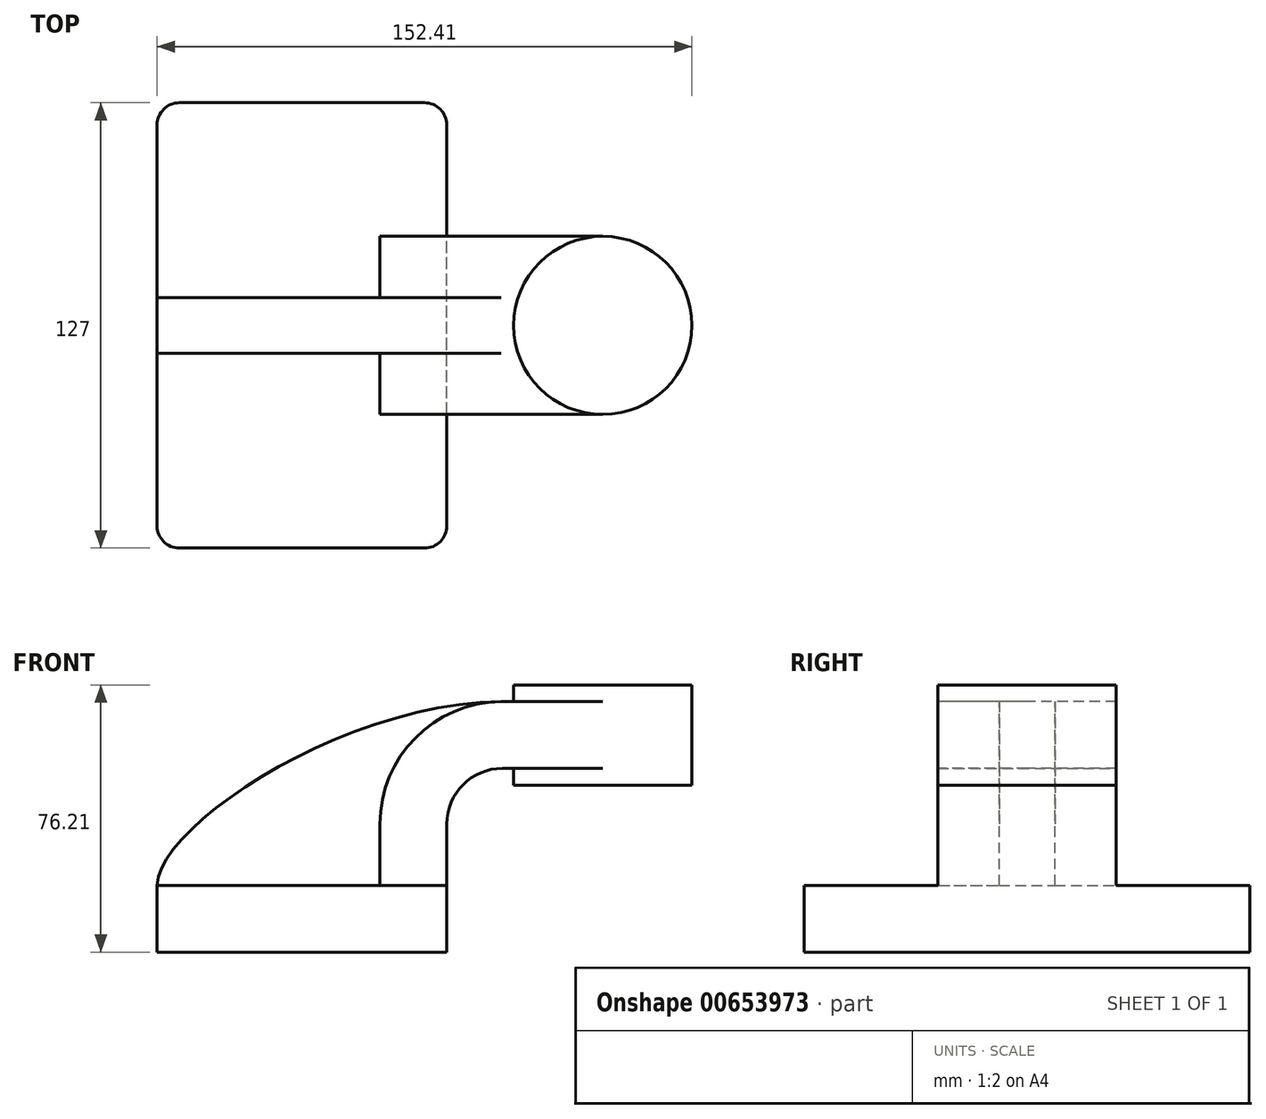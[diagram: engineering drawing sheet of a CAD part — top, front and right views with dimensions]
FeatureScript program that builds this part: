
annotation { "Feature Type Name" : "Feature", "Feature Type Description" : "" }
export const myFeature = defineFeature(function(context is Context, id is Id, definition is map)
    precondition{}
    {
        {
            var Q0;
            Q0=qCreatedBy(makeId("Front.planeOp"),FACE);
            var sketch = newSketch(context, id + "F0", { "sketchPlane" : qUnion([Q0])});
            skLineSegment(sketch, "E0.bottom", {"start": v(-41.28, -9.53) * mm, "end": v(41.28, -9.53) * mm});
            skLineSegment(sketch, "E0.top", {"start": v(-41.28, 9.52) * mm, "end": v(41.28, 9.52) * mm});
            skLineSegment(sketch, "E0.left", {"start": v(-41.28, -9.53) * mm, "end": v(-41.28, 9.53) * mm});
            skLineSegment(sketch, "E0.right", {"start": v(41.28, -9.53) * mm, "end": v(41.28, 9.52) * mm});
            skPoint(sketch, "E0.middle", {"position": v(0, 0) * mm});
            skLineSegment(sketch, "E1.bottom", {"start": v(60.33, 38.1) * mm, "end": v(111.12, 38.1) * mm});
            skLineSegment(sketch, "E1.top", {"start": v(60.32, 66.67) * mm, "end": v(111.12, 66.67) * mm});
            skLineSegment(sketch, "E1.left", {"start": v(60.33, 38.1) * mm, "end": v(60.32, 66.68) * mm});
            skLineSegment(sketch, "E1.right", {"start": v(111.12, 38.1) * mm, "end": v(111.12, 66.68) * mm});
            skPoint(sketch, "E1.middle", {"position": v(85.72, 52.39) * mm});
            skLineSegment(sketch, "E2", {"start": v(41.27, 9.52) * mm, "end": v(41.27, 27) * mm});
            skArc(sketch, "E3", {"start": v(41.27, 27) * mm, "mid": v(45.92, 38.23) * mm, "end": v(57.15, 42.88) * mm});
            skLineSegment(sketch, "E4", {"start": v(57.15, 42.88) * mm, "end": v(85.72, 42.88) * mm});
            skLineSegment(sketch, "E5", {"start": v(85.72, 38.1) * mm, "end": v(85.72, 66.67) * mm});
            skLineSegment(sketch, "E6.0", {"start": v(57.15, 61.93) * mm, "end": v(85.72, 61.93) * mm});
            skArc(sketch, "E6.1", {"start": v(22.23, 27) * mm, "mid": v(32.45, 51.7) * mm, "end": v(57.15, 61.93) * mm});
            skLineSegment(sketch, "E6.2", {"start": v(22.22, 9.52) * mm, "end": v(22.22, 27) * mm});
            skFitSpline(sketch, "E7", {"points": [v(-41.28, 9.53) * mm, v(57.15, 61.93) * mm], "startDerivative": vector(0.78, 50.8) * mm, "endDerivative": vector(135.68, 0.52) * mm});
            skSolve(sketch);
        }
        {
            var Q0;
            Q0=makeQuery(id+"F0.imprint","IMPRINT",FACE,{"disambiguationData":[TD([[makeQuery(id+"F0.imprint","IMPRINT",EDGE,{"derivedFrom":sQuery(id+"F0.wireOp",EDGE,"E0.bottom")}),1.0]])]});
            extrude(context, id + "F1", {"entities" : qUnion([Q0]), "endBound" : BoundingType.SYMMETRIC, "depth" : 127 * mm, "offsetDistance" : 25.4 * mm});
        }
        {
            var Q0;
            {var subQ1=sQuery(id+"F0.wireOp",EDGE,"E2");Q0=makeQuery(id+"F0.imprint","IMPRINT",FACE,{"disambiguationData":[TD([[makeQuery(id+"F0.imprint","IMPRINT",EDGE,{"derivedFrom":subQ1}),1.0]])]});}
            var Q1;
            {var subQ0=sQuery(id+"F0.wireOp",EDGE,"E4");var subQ1=sQuery(id+"F0.wireOp",EDGE,"E1.left");var subQ2=makeQuery(id+"F0.imprint","INTERSECT",VERTEX,{"derivedFrom":[subQ1,subQ0]});Q1=makeQuery(id+"F0.imprint","IMPRINT",FACE,{"disambiguationData":[TD([[makeQuery(id+"F0.imprint","IMPRINT",EDGE,{"disambiguationData":[TD([[subQ2,-1.0]])],"derivedFrom":subQ1}),-1.0]])]});}
            extrude(context, id + "F2", {"entities" : qUnion([Q0, Q1]), "operationType" : NewBodyOperationType.ADD, "endBound" : BoundingType.SYMMETRIC, "depth" : 50.8 * mm, "offsetDistance" : 25.4 * mm});
        }
        {
            var Q0;
            {var subQ3=sQuery(id+"F0.wireOp",EDGE,"E6.2");Q0=makeQuery(id+"F0.imprint","IMPRINT",FACE,{"disambiguationData":[TD([[makeQuery(id+"F0.imprint","IMPRINT",EDGE,{"derivedFrom":subQ3}),1.0]])]});}
            extrude(context, id + "F3", {"entities" : qUnion([Q0]), "operationType" : NewBodyOperationType.ADD, "endBound" : BoundingType.SYMMETRIC, "depth" : 15.88 * mm, "offsetDistance" : 25.4 * mm});
        }
        {
            var Q0;
            {var subQ4=sQuery(id+"F0.wireOp",EDGE,"E1.right");Q0=makeQuery(id+"F0.imprint","IMPRINT",FACE,{"disambiguationData":[TD([[makeQuery(id+"F0.imprint","IMPRINT",EDGE,{"derivedFrom":subQ4}),1.0]])]});}
            var Q1;
            Q1=sQuery(id+"F0.wireOp",EDGE,"E5");
            revolve(context, id + "F4", {"operationType" : NewBodyOperationType.ADD, "entities" : qUnion([Q0]), "axis" : qUnion([Q1]), "revolveType" : RevolveType.FULL});
        }
        {
            var Q0;
            Q0=makeQuery(id+"F1.opExtrude","CAP_EDGE",EDGE,{"disambiguationData":[OSD([sQuery(id+"F0.wireOp",EDGE,"E0.left")])],"isStart":false});
            var Q1;
            Q1=makeQuery(id+"F1.opExtrude","CAP_EDGE",EDGE,{"disambiguationData":[OSD([sQuery(id+"F0.wireOp",EDGE,"E0.right")])],"isStart":false});
            var Q2;
            Q2=makeQuery(id+"F1.opExtrude","CAP_EDGE",EDGE,{"disambiguationData":[OSD([sQuery(id+"F0.wireOp",EDGE,"E0.right")])],"isStart":true});
            var Q3;
            Q3=makeQuery(id+"F1.opExtrude","CAP_EDGE",EDGE,{"disambiguationData":[OSD([sQuery(id+"F0.wireOp",EDGE,"E0.left")])],"isStart":true});
            fillet(context, id + "F5", {"entities" : qUnion([Q0, Q1, Q2, Q3]), "radius" : 6.35 * mm, "tangentPropagation" : true, "allowEdgeOverflow" : false});
        }
    });
